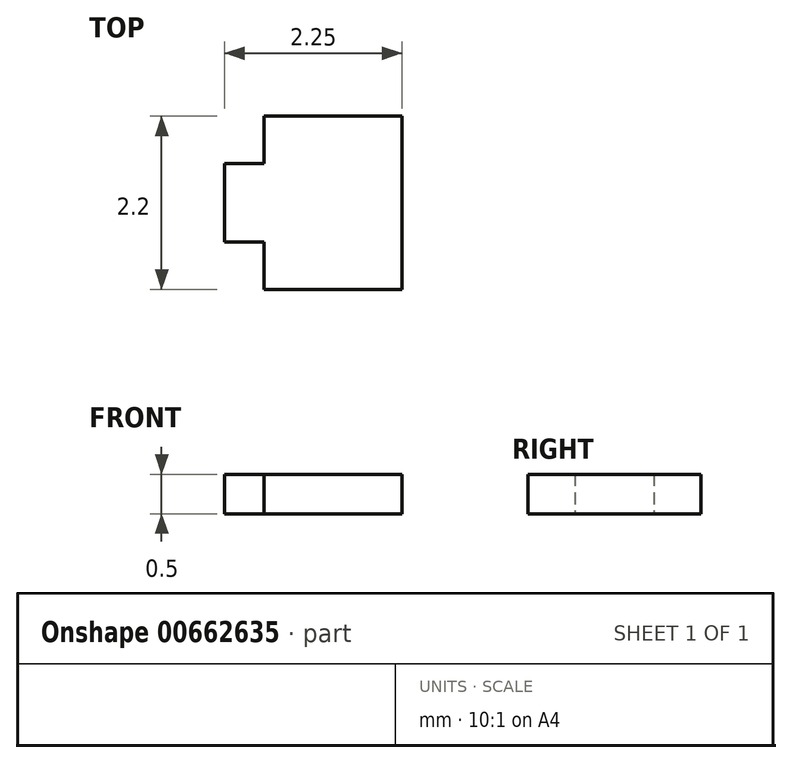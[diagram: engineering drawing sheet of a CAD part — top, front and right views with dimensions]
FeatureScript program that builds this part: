
annotation { "Feature Type Name" : "Feature", "Feature Type Description" : "" }
export const myFeature = defineFeature(function(context is Context, id is Id, definition is map)
    precondition{}
    {
        {
            var Q0;
            Q0=qCreatedBy(makeId("Top.planeOp"),FACE);
            var sketch = newSketch(context, id + "F0", { "sketchPlane" : qUnion([Q0])});
            skLineSegment(sketch, "E0.bottom", {"start": v(0, 0.5) * mm, "end": v(0.5, 0.5) * mm});
            skLineSegment(sketch, "E1.bottom", {"start": v(0.5, 1.1) * mm, "end": v(2.25, 1.1) * mm});
            skLineSegment(sketch, "E1.left", {"start": v(0.5, 1.1) * mm, "end": v(0.5, 0.5) * mm});
            skLineSegment(sketch, "E2.MirrorCS", {"start": v(0.5, -1.1) * mm, "end": v(2.25, -1.1) * mm});
            skLineSegment(sketch, "E3.MirrorCS", {"start": v(0.5, -1.1) * mm, "end": v(0.5, -0.5) * mm});
            skLineSegment(sketch, "E4.MirrorCS", {"start": v(0, -0.5) * mm, "end": v(0.5, -0.5) * mm});
            skLineSegment(sketch, "E5", {"start": v(2.25, 1.1) * mm, "end": v(2.25, -1.1) * mm});
            skLineSegment(sketch, "E6", {"start": v(0, 0.5) * mm, "end": v(0, -0.5) * mm});
            skSolve(sketch);
        }
        {
            var Q0;
            Q0=makeQuery(id+"F0.imprint","IMPRINT",FACE,{"disambiguationData":[TD([[makeQuery(id+"F0.imprint","IMPRINT",EDGE,{"derivedFrom":sQuery(id+"F0.wireOp",EDGE,"E0.bottom")}),-1.0]])]});
            extrude(context, id + "F1", {"entities" : qUnion([Q0]), "depth" : .5 * mm, "offsetDistance" : 25 * mm});
        }
    });
